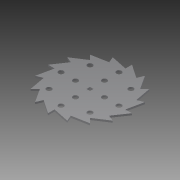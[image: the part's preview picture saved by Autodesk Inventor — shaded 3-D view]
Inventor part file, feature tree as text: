
AUTODESK INVENTOR PART (.ipt)
format: ipt  version: 2014 SP1 (Build 180222100, 222)  size: 675,840 bytes
history: native  units: in
note: dims shown in document units (in); Inventor stores cm internally (conversion verified against a paired STEP export)
features: extrude x6, sketch x6, other x1, imported_body x1, pattern_circular x1, projected_geometry x1
ambient origin geometry x8: Origin, YZ Plane, XZ Plane, XY Plane, X Axis, Y Axis, Z Axis, Center Point
bodies: Body1 (feature_tree)
feature tree (16):
  parser-record x1  (decoder bookkeeping rows leaked as tree rows — omitted from the tree; the rows remain in map.json)
  imported_body  "Base1"
  extrude  "Extrusion1"  Depth=1.0in TaperAngle=0.0deg
  extrude  "Extrusion2"  Depth=1.0in TaperAngle=0.0deg
  extrude  "Extrusion4"  Depth=1.0in TaperAngle=0.0deg
  pattern_circular  "Circular Pattern1"  [2 undecoded]
  extrude  "Extrusion6"  [1 undecoded]
  extrude  "Extrusion7"  [1 undecoded]
  extrude  "Extrusion8"  [1 undecoded]
  sketch  "Sketch1"  dims[d0=1.0in d1=0.0in d2=1.0in d3=0.0in]
  sketch  "Sketch2"  dims[d18=0.253in d19=1.0in d20=0.0in]
  sketch  "Sketch6"  dims[d21=6.2992in d22=360.0deg d26=1.0in d27=0.0in]
  sketch  "Sketch8"  dims[d28=0.0625in d29=0.0in]
  projected_geometry  "Projected Loop1"
  sketch  "Sketch9"  dims[d30=0.121in]
  sketch  "Sketch10"  dims[d31=0.121in d32=0.0625in d33=0.0in]
note: 5 required parameter values undecoded (feature->parameter linkage not recoverable at this tier; creation-order binding heuristic only, values carry confidence <= 0.55)
